# Revit family: Cumberland-Ovid-Lounge
name_source: partatom
category: Furniture
revit_build: Autodesk Revit 2014 (Build: 20130308_1515(x64)
units: mm (PartAtom-declared; Revit-internal decimal feet)

## types (3) — shared parameters
Arm Finish = CUM - Linen - Beige
Assembly Code = E2020200
Back Finish = CUM - Linen - Beige
Depth = 28 11/16"
Height = 29 7/8"
Keynote = 12500
Leg Finish = CUM - UHMW, Black
Low Emitting Finish = Yes
Low Emitting Material = Yes
Manufacturer = Cumberland
Salvage or Reuse = Yes
Seat Finish = CUM - Linen - Beige
Type Comments = Ovid
URL = www.cumberlandfurniture.com
zero-valued in all types: Percentage of Recycled Content

## per-type parameters (varying)
| type | Cut | Description | Line C | Width |
| 10-1200 | 38 7/8" | Ovid 27"W 29.5"H 29"D | No | 28" |
| 10-1201 | 32 7/8" | Ovid 78"W 29.5"H 29"D | Yes | 78" |
| 10-1202 | 32 7/8" | Ovid 90"W 29.5"H 29"D | Yes | 90" |

note: column(s) folded — value = type name in every type: Model

## geometry (parser evidence)
native form markers: Sweep x5
no freeform markers — native parametric forms only
